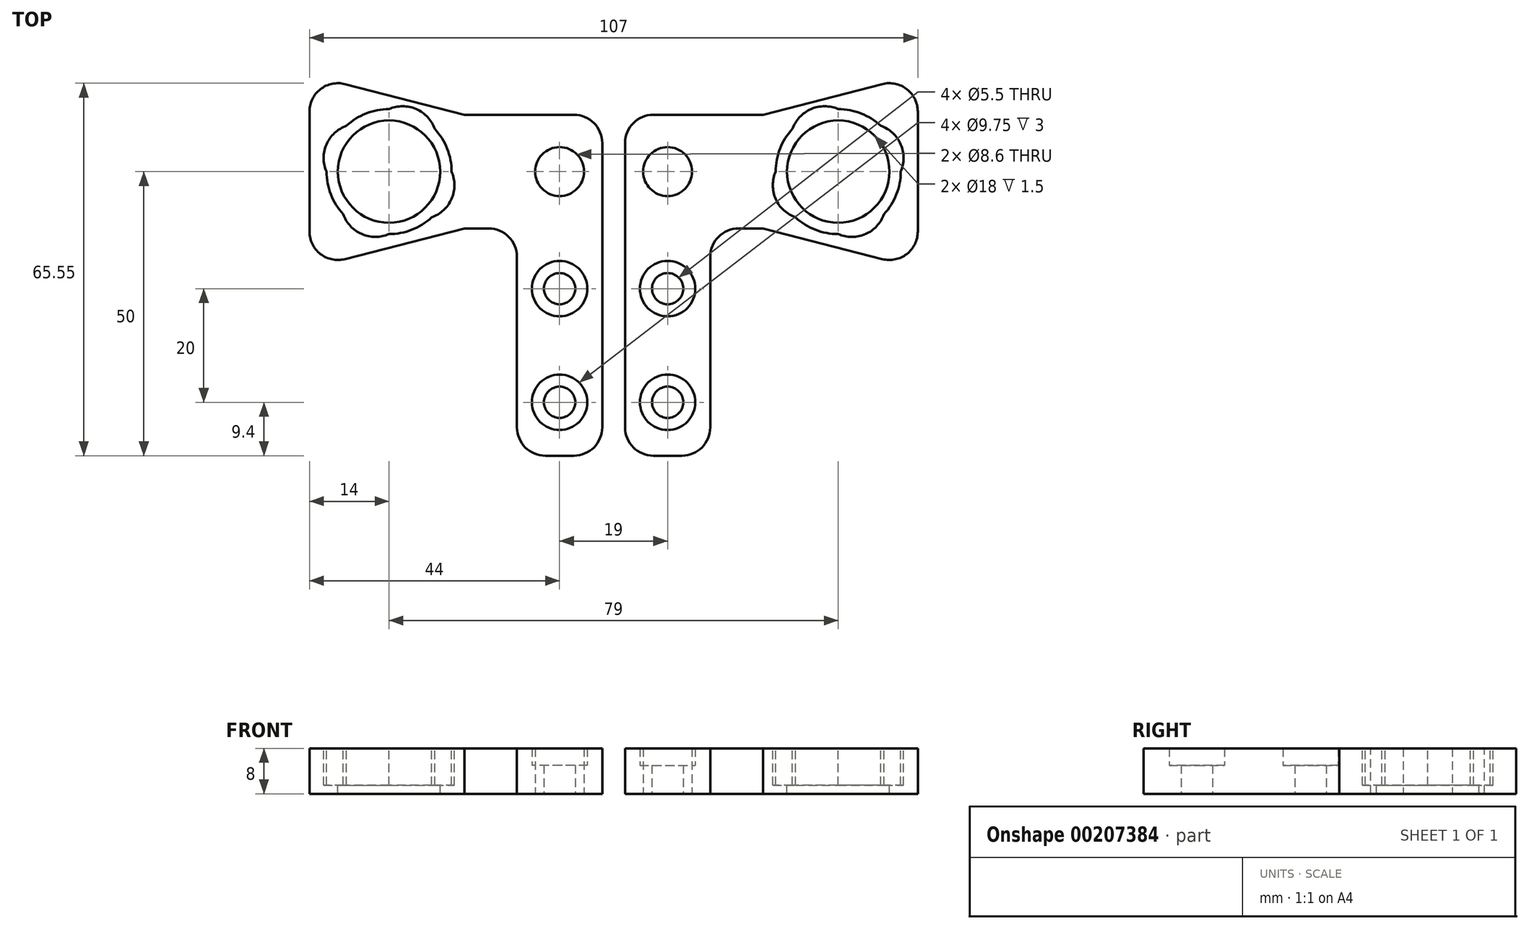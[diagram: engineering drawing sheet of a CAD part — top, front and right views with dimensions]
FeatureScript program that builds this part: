
annotation { "Feature Type Name" : "Feature", "Feature Type Description" : "" }
export const myFeature = defineFeature(function(context is Context, id is Id, definition is map)
    precondition{}
    {
        {
            var Q0;
            Q0=qCreatedBy(makeId("Top.planeOp"),FACE);
            var sketch = newSketch(context, id + "F0", { "sketchPlane" : qUnion([Q0])});
            skPoint(sketch, "E0", {"position": v(39.5, 50) * mm});
            skLineSegment(sketch, "E1.right", {"start": v(53.5, 67) * mm, "end": v(53.5, 33) * mm});
            skLineSegment(sketch, "E2", {"start": v(9.5, 29.4) * mm, "end": v(9.5, 9.4) * mm, "construction": true});
            skPoint(sketch, "E3", {"position": v(9.5, 19.4) * mm});
            skLineSegment(sketch, "E4.top", {"start": v(2, 0) * mm, "end": v(17, 0) * mm});
            skLineSegment(sketch, "E4.right", {"start": v(17, 40) * mm, "end": v(17, 0) * mm});
            skPoint(sketch, "E5", {"position": v(17, 19.4) * mm});
            skPoint(sketch, "E6", {"position": v(9.5, 0) * mm});
            skPoint(sketch, "E7", {"position": v(9.5, 29.4) * mm});
            skPoint(sketch, "E8", {"position": v(9.5, 9.4) * mm});
            skPoint(sketch, "E9", {"position": v(9.5, 50) * mm});
            skPoint(sketch, "E10", {"position": v(53.5, 50) * mm});
            skPoint(sketch, "E11", {"position": v(26.25, 60) * mm});
            skPoint(sketch, "E12", {"position": v(26.25, 40) * mm});
            skLineSegment(sketch, "E13", {"start": v(2, 60) * mm, "end": v(26.25, 60) * mm});
            skLineSegment(sketch, "E14", {"start": v(26.25, 60) * mm, "end": v(53.5, 67) * mm});
            skLineSegment(sketch, "E15", {"start": v(17, 40) * mm, "end": v(26.25, 40) * mm});
            skLineSegment(sketch, "E16", {"start": v(26.25, 40) * mm, "end": v(53.5, 33) * mm});
            skLineSegment(sketch, "E17", {"start": v(2, 40) * mm, "end": v(2, 60) * mm});
            skLineSegment(sketch, "E18", {"start": v(2, 40) * mm, "end": v(2, 0) * mm});
            skPoint(sketch, "E19", {"position": v(2, 50) * mm});
            skCircle(sketch, "E20", {"center": v(39.5, 50) * mm, "radius": 11 * mm});
            skCircle(sketch, "E21.0", {"center": v(39.5, 50) * mm, "radius": 9 * mm});
            skCircle(sketch, "E22", {"center": v(37.1, 55.5) * mm, "radius": 6 * mm});
            skPoint(sketch, "E22.second.point", {"position": v(31.44, 57.49) * mm});
            skPoint(sketch, "E22.third.point", {"position": v(39.5, 61) * mm});
            skCircle(sketch, "E23.1.0", {"center": v(34, 47.6) * mm, "radius": 6 * mm});
            skCircle(sketch, "E23.2.0", {"center": v(41.9, 44.5) * mm, "radius": 6 * mm});
            skCircle(sketch, "E23.3.0", {"center": v(45, 52.4) * mm, "radius": 6 * mm});
            skSolve(sketch);
        }
        {
            var Q0;
            Q0=makeQuery(id+"F0.imprint","IMPRINT",FACE,{"disambiguationData":[TD([[makeQuery(id+"F0.imprint","IMPRINT",EDGE,{"derivedFrom":sQuery(id+"F0.wireOp",EDGE,"E1.right")}),-1.0]])]});
            var Q1;
            {var subQ0=sQuery(id+"F0.wireOp",EDGE,"E4.top");Q1=makeQuery(id+"F0.imprint","IMPRINT",FACE,{"disambiguationData":[TD([[makeQuery(id+"F0.imprint","IMPRINT",EDGE,{"derivedFrom":subQ0}),1.0]])]});}
            extrude(context, id + "F1", {"entities" : qUnion([Q0, Q1]), "oppositeDirection" : true, "depth" : 8 * mm, "offsetDistance" : 25 * mm});
        }
        {
            var Q0;
            Q0=sQuery(id+"F0.wireOp",VERTEX,"E9");
            var Q1;
            Q1=makeQuery(id+"F1.opExtrude","SWEPT_BODY",BODY,{"disambiguationData":[OSD([sQuery(id+"F0.wireOp",EDGE,"E1.right"),sQuery(id+"F0.wireOp",EDGE,"E4.top"),sQuery(id+"F0.wireOp",EDGE,"E4.left"),sQuery(id+"F0.wireOp",EDGE,"E4.right"),sQuery(id+"F0.wireOp",EDGE,"lUboI7vS-MJ5s-rvf2-cX16-rLJiyycNvOs9"),sQuery(id+"F0.wireOp",EDGE,"j1iU3DaQ-BT0G-V7HJ-mhui-iUxERosTZKM6")])]});
            hole(context, id + "F2", {"style" : HoleStyle.SIMPLE, "endStyle" : HoleEndStyle.THROUGH, "holeDiameter" : 8.6 * mm, "majorDiameter" : 5 * mm, "isTappedThrough" : true, "tappedDepth" : 12 * mm, "tapClearance" : 3, "locations" : qUnion([Q0]), "scope" : qUnion([Q1]), "startStyle" : HoleStartStyle.SKETCH});
        }
        {
            var Q0;
            Q0=sQuery(id+"F0.wireOp",VERTEX,"E7");
            var Q1;
            Q1=sQuery(id+"F0.wireOp",VERTEX,"E8");
            var Q2;
            Q2=makeQuery(id+"F1.opExtrude","SWEPT_BODY",BODY,{"disambiguationData":[OSD([sQuery(id+"F0.wireOp",EDGE,"E1.right"),sQuery(id+"F0.wireOp",EDGE,"E4.top"),sQuery(id+"F0.wireOp",EDGE,"E4.left"),sQuery(id+"F0.wireOp",EDGE,"E4.right"),sQuery(id+"F0.wireOp",EDGE,"lUboI7vS-MJ5s-rvf2-cX16-rLJiyycNvOs9"),sQuery(id+"F0.wireOp",EDGE,"j1iU3DaQ-BT0G-V7HJ-mhui-iUxERosTZKM6")])]});
            hole(context, id + "F3", {"style" : HoleStyle.C_BORE, "endStyle" : HoleEndStyle.THROUGH, "holeDiameter" : 5.5 * mm, "cBoreDiameter" : 9.75 * mm, "cBoreDepth" : 3 * mm, "majorDiameter" : 5 * mm, "isTappedThrough" : true, "tappedDepth" : 12 * mm, "tapClearance" : 3, "locations" : qUnion([Q0, Q1]), "scope" : qUnion([Q2]), "startStyle" : HoleStartStyle.SKETCH});
        }
        {
            var Q0;
            Q0=makeQuery(id+"F1.opExtrude","SWEPT_EDGE",EDGE,{"disambiguationData":[OSD([sQuery(id+"F0.wireOp",EDGE,"E4.top"),sQuery(id+"F0.wireOp",EDGE,"E4.right")])]});
            var Q1;
            Q1=makeQuery(id+"F1.opExtrude","SWEPT_EDGE",EDGE,{"disambiguationData":[OSD([sQuery(id+"F0.wireOp",EDGE,"E4.top"),sQuery(id+"F0.wireOp",EDGE,"E4.left")])]});
            var Q2;
            Q2=makeQuery(id+"F1.opExtrude","SWEPT_EDGE",EDGE,{"disambiguationData":[OSD([sQuery(id+"F0.wireOp",EDGE,"E4.left"),sQuery(id+"F0.wireOp",EDGE,"j1iU3DaQ-BT0G-V7HJ-mhui-iUxERosTZKM6")])]});
            var Q3;
            Q3=makeQuery(id+"F1.opExtrude","SWEPT_EDGE",EDGE,{"disambiguationData":[OSD([sQuery(id+"F0.wireOp",EDGE,"E1.right"),sQuery(id+"F0.wireOp",EDGE,"j1iU3DaQ-BT0G-V7HJ-mhui-iUxERosTZKM6")])]});
            var Q4;
            Q4=makeQuery(id+"F1.opExtrude","SWEPT_EDGE",EDGE,{"disambiguationData":[OSD([sQuery(id+"F0.wireOp",EDGE,"E1.right"),sQuery(id+"F0.wireOp",EDGE,"lUboI7vS-MJ5s-rvf2-cX16-rLJiyycNvOs9")])]});
            var Q5;
            Q5=makeQuery(id+"F1.opExtrude","SWEPT_EDGE",EDGE,{"disambiguationData":[OSD([sQuery(id+"F0.wireOp",EDGE,"E4.right"),sQuery(id+"F0.wireOp",EDGE,"lUboI7vS-MJ5s-rvf2-cX16-rLJiyycNvOs9"),sQuery(id+"F0.wireOp",EDGE,"JXlcmhnK-QmtE-nQg1-gXyn-2xB9LDxkqaOU")])]});
            var Q6;
            Q6=makeQuery(id+"F1.opExtrude","SWEPT_EDGE",EDGE,{"disambiguationData":[OSD([sQuery(id+"F0.wireOp",EDGE,"E13"),sQuery(id+"F0.wireOp",EDGE,"E17")])]});
            fillet(context, id + "F4", {"entities" : qUnion([Q0, Q1, Q2, Q3, Q4, Q5, Q6]), "radius" : 5 * mm, "tangentPropagation" : true, "allowEdgeOverflow" : false});
        }
        {
            var Q0;
            {var subQ0=sQuery(id+"F0.wireOp",EDGE,"E22");var subQ1=sQuery(id+"F0.wireOp",EDGE,"E20");var subQ2=makeQuery(id+"F0.imprint","INTERSECT",VERTEX,{"disambiguationData":[OD(0.0)],"derivedFrom":[subQ1,subQ0]});Q0=makeQuery(id+"F0.imprint","IMPRINT",FACE,{"disambiguationData":[TD([[makeQuery(id+"F0.imprint","IMPRINT",EDGE,{"disambiguationData":[TD([[subQ2,-1.0]])],"derivedFrom":subQ1}),1.0]])]});}
            var Q1;
            {var subQ0=sQuery(id+"F0.wireOp",EDGE,"E22");var subQ1=sQuery(id+"F0.wireOp",EDGE,"E20");var subQ2=makeQuery(id+"F0.imprint","INTERSECT",VERTEX,{"disambiguationData":[OD(0.0)],"derivedFrom":[subQ1,subQ0]});Q1=makeQuery(id+"F0.imprint","IMPRINT",FACE,{"disambiguationData":[TD([[makeQuery(id+"F0.imprint","IMPRINT",EDGE,{"disambiguationData":[TD([[subQ2,-1.0]])],"derivedFrom":subQ1}),-1.0]])]});}
            var Q2;
            {var subQ0=sQuery(id+"F0.wireOp",EDGE,"E23.3.0");var subQ1=sQuery(id+"F0.wireOp",EDGE,"E20");var subQ2=makeQuery(id+"F0.imprint","INTERSECT",VERTEX,{"disambiguationData":[OD(0.0)],"derivedFrom":[subQ1,subQ0]});Q2=makeQuery(id+"F0.imprint","IMPRINT",FACE,{"disambiguationData":[TD([[makeQuery(id+"F0.imprint","IMPRINT",EDGE,{"disambiguationData":[TD([[subQ2,-1.0]])],"derivedFrom":subQ1}),1.0]])]});}
            var Q3;
            {var subQ0=sQuery(id+"F0.wireOp",EDGE,"E23.3.0");var subQ1=sQuery(id+"F0.wireOp",EDGE,"E20");var subQ2=makeQuery(id+"F0.imprint","INTERSECT",VERTEX,{"disambiguationData":[OD(0.0)],"derivedFrom":[subQ1,subQ0]});Q3=makeQuery(id+"F0.imprint","IMPRINT",FACE,{"disambiguationData":[TD([[makeQuery(id+"F0.imprint","IMPRINT",EDGE,{"disambiguationData":[TD([[subQ2,1.0]])],"derivedFrom":subQ1}),1.0]])]});}
            var Q4;
            {var subQ0=sQuery(id+"F0.wireOp",EDGE,"E23.3.0");var subQ1=sQuery(id+"F0.wireOp",EDGE,"E20");var subQ2=makeQuery(id+"F0.imprint","INTERSECT",VERTEX,{"disambiguationData":[OD(0.0)],"derivedFrom":[subQ1,subQ0]});Q4=makeQuery(id+"F0.imprint","IMPRINT",FACE,{"disambiguationData":[TD([[makeQuery(id+"F0.imprint","IMPRINT",EDGE,{"disambiguationData":[TD([[subQ2,1.0]])],"derivedFrom":subQ1}),-1.0]])]});}
            var Q5;
            {var subQ0=sQuery(id+"F0.wireOp",EDGE,"E23.3.0");var subQ1=sQuery(id+"F0.wireOp",EDGE,"E20");var subQ2=makeQuery(id+"F0.imprint","INTERSECT",VERTEX,{"disambiguationData":[OD(1.0)],"derivedFrom":[subQ1,subQ0]});Q5=makeQuery(id+"F0.imprint","IMPRINT",FACE,{"disambiguationData":[TD([[makeQuery(id+"F0.imprint","IMPRINT",EDGE,{"disambiguationData":[TD([[subQ2,1.0]])],"derivedFrom":subQ1}),1.0]])]});}
            var Q6;
            {var subQ0=sQuery(id+"F0.wireOp",EDGE,"E23.2.0");var subQ1=sQuery(id+"F0.wireOp",EDGE,"E20");var subQ2=makeQuery(id+"F0.imprint","INTERSECT",VERTEX,{"disambiguationData":[OD(0.0)],"derivedFrom":[subQ1,subQ0]});Q6=makeQuery(id+"F0.imprint","IMPRINT",FACE,{"disambiguationData":[TD([[makeQuery(id+"F0.imprint","IMPRINT",EDGE,{"disambiguationData":[TD([[subQ2,-1.0]])],"derivedFrom":subQ1}),1.0]])]});}
            var Q7;
            {var subQ0=sQuery(id+"F0.wireOp",EDGE,"E23.2.0");var subQ1=sQuery(id+"F0.wireOp",EDGE,"E20");var subQ2=makeQuery(id+"F0.imprint","INTERSECT",VERTEX,{"disambiguationData":[OD(0.0)],"derivedFrom":[subQ1,subQ0]});Q7=makeQuery(id+"F0.imprint","IMPRINT",FACE,{"disambiguationData":[TD([[makeQuery(id+"F0.imprint","IMPRINT",EDGE,{"disambiguationData":[TD([[subQ2,-1.0]])],"derivedFrom":subQ1}),-1.0]])]});}
            var Q8;
            {var subQ0=sQuery(id+"F0.wireOp",EDGE,"E23.1.0");var subQ1=sQuery(id+"F0.wireOp",EDGE,"E20");var subQ2=makeQuery(id+"F0.imprint","INTERSECT",VERTEX,{"disambiguationData":[OD(1.0)],"derivedFrom":[subQ1,subQ0]});Q8=makeQuery(id+"F0.imprint","IMPRINT",FACE,{"disambiguationData":[TD([[makeQuery(id+"F0.imprint","IMPRINT",EDGE,{"disambiguationData":[TD([[subQ2,-1.0]])],"derivedFrom":subQ1}),1.0]])]});}
            var Q9;
            {var subQ0=sQuery(id+"F0.wireOp",EDGE,"E23.1.0");var subQ1=sQuery(id+"F0.wireOp",EDGE,"E20");var subQ2=makeQuery(id+"F0.imprint","INTERSECT",VERTEX,{"disambiguationData":[OD(0.0)],"derivedFrom":[subQ1,subQ0]});Q9=makeQuery(id+"F0.imprint","IMPRINT",FACE,{"disambiguationData":[TD([[makeQuery(id+"F0.imprint","IMPRINT",EDGE,{"disambiguationData":[TD([[subQ2,-1.0]])],"derivedFrom":subQ1}),1.0]])]});}
            var Q10;
            {var subQ0=sQuery(id+"F0.wireOp",EDGE,"E23.1.0");var subQ1=sQuery(id+"F0.wireOp",EDGE,"E20");var subQ2=makeQuery(id+"F0.imprint","INTERSECT",VERTEX,{"disambiguationData":[OD(0.0)],"derivedFrom":[subQ1,subQ0]});Q10=makeQuery(id+"F0.imprint","IMPRINT",FACE,{"disambiguationData":[TD([[makeQuery(id+"F0.imprint","IMPRINT",EDGE,{"disambiguationData":[TD([[subQ2,-1.0]])],"derivedFrom":subQ1}),-1.0]])]});}
            var Q11;
            {var subQ0=sQuery(id+"F0.wireOp",EDGE,"E22");var subQ1=sQuery(id+"F0.wireOp",EDGE,"E20");var subQ2=makeQuery(id+"F0.imprint","INTERSECT",VERTEX,{"disambiguationData":[OD(1.0)],"derivedFrom":[subQ1,subQ0]});Q11=makeQuery(id+"F0.imprint","IMPRINT",FACE,{"disambiguationData":[TD([[makeQuery(id+"F0.imprint","IMPRINT",EDGE,{"disambiguationData":[TD([[subQ2,-1.0]])],"derivedFrom":subQ1}),1.0]])]});}
            extrude(context, id + "F5", {"entities" : qUnion([Q0, Q1, Q2, Q3, Q4, Q5, Q6, Q7, Q8, Q9, Q10, Q11]), "operationType" : NewBodyOperationType.ADD, "oppositeDirection" : true, "depth" : 8 * mm, "offsetDistance" : 25 * mm, "hasSecondDirection" : true, "secondDirectionOppositeDirection" : true, "secondDirectionDepth" : 6.5 * mm});
        }
        {
            var Q0;
            Q0=makeQuery(id+"F1.opExtrude","SWEPT_BODY",BODY,{"disambiguationData":[OSD([sQuery(id+"F0.wireOp",EDGE,"E1.right"),sQuery(id+"F0.wireOp",EDGE,"E4.left"),sQuery(id+"F0.wireOp",EDGE,"lUboI7vS-MJ5s-rvf2-cX16-rLJiyycNvOs9"),sQuery(id+"F0.wireOp",EDGE,"j1iU3DaQ-BT0G-V7HJ-mhui-iUxERosTZKM6"),sQuery(id+"F0.wireOp",EDGE,"JXlcmhnK-QmtE-nQg1-gXyn-2xB9LDxkqaOU")])]});
            var Q1;
            Q1=qCreatedBy(makeId("Right.planeOp"),FACE);
            mirror(context, id + "F6", {"entities" : qUnion([Q0]), "mirrorPlane" : qUnion([Q1])});
        }
    });
